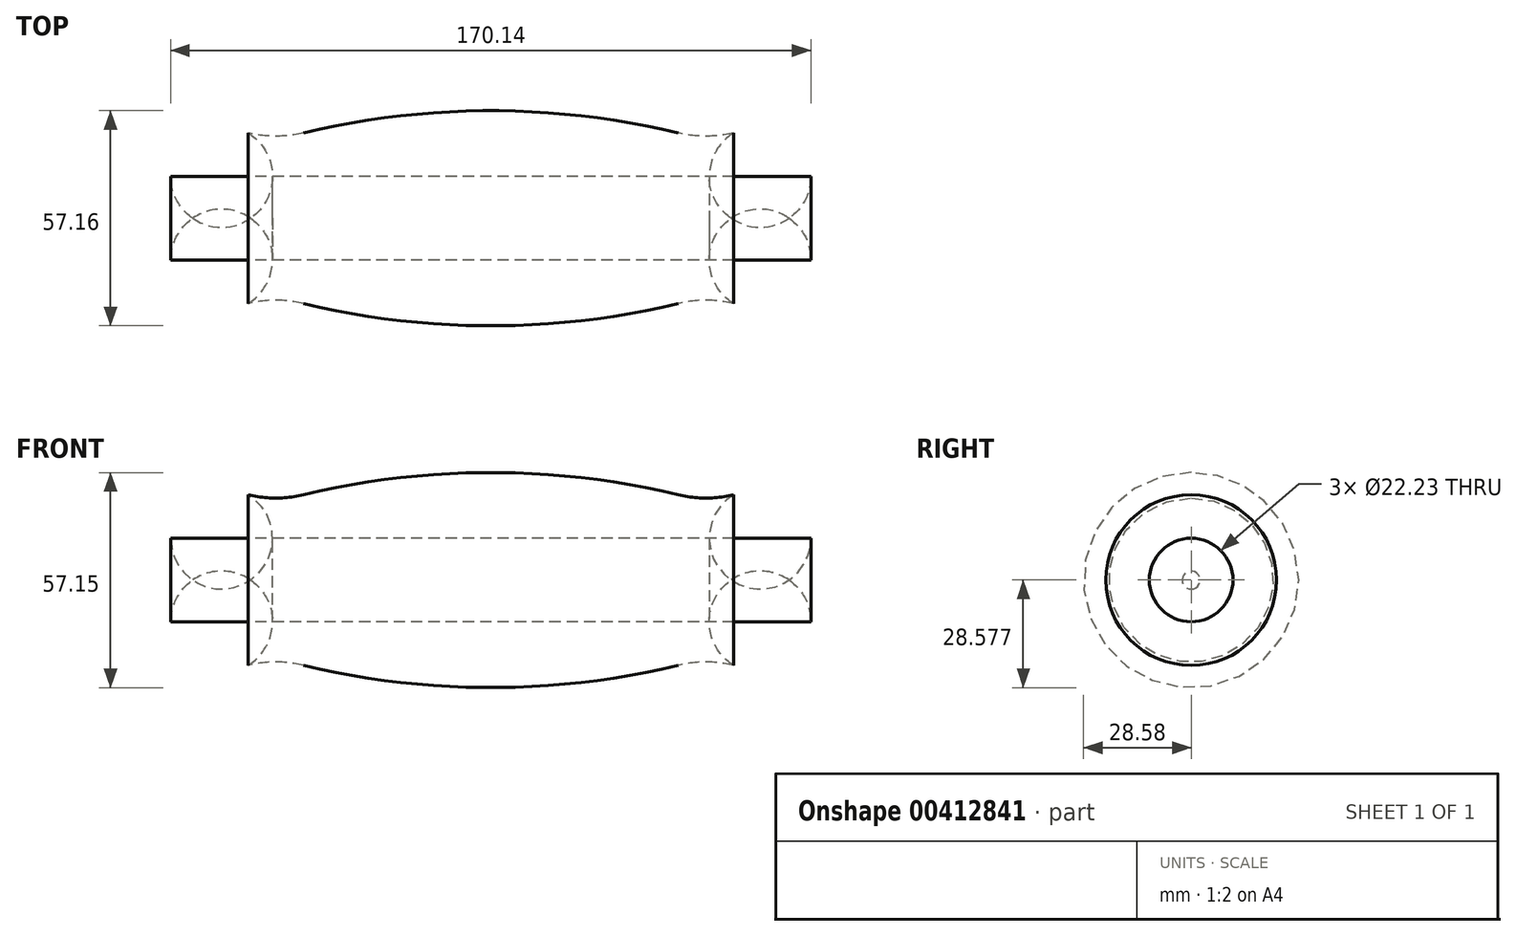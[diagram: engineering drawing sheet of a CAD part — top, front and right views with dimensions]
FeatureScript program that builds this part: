
annotation { "Feature Type Name" : "Feature", "Feature Type Description" : "" }
export const myFeature = defineFeature(function(context is Context, id is Id, definition is map)
    precondition{}
    {
        {
            var Q0;
            Q0=qCreatedBy(makeId("Front.planeOp"),FACE);
            var sketch = newSketch(context, id + "F0", { "sketchPlane" : qUnion([Q0])});
            skLineSegment(sketch, "E0", {"start": v(-49.73, 0) * mm, "end": v(12.26, 0) * mm, "construction": true});
            skArc(sketch, "E1", {"start": v(-49.73, 11.57) * mm, "mid": v(-25.04, 15.98) * mm, "end": v(0, 17.46) * mm});
            skArc(sketch, "E2", {"start": v(-49.73, 11.57) * mm, "mid": v(-57.15, 10.69) * mm, "end": v(-64.57, 11.57) * mm});
            skArc(sketch, "E3", {"start": v(-64.57, 11.57) * mm, "mid": v(-78.2, 11.77) * mm, "end": v(-85.07, 0) * mm});
            skLineSegment(sketch, "E4", {"start": v(-41.18, -11.11) * mm, "end": v(0, -11.11) * mm, "construction": true});
            skLineSegment(sketch, "E5", {"start": v(0, -11.11) * mm, "end": v(0, 44.87) * mm, "construction": true});
            skLineSegment(sketch, "E6", {"start": v(-85.07, 0) * mm, "end": v(0, 0) * mm});
            skArc(sketch, "E7.MirrorCS", {"start": v(49.73, 11.57) * mm, "mid": v(25.04, 15.98) * mm, "end": v(0, 17.46) * mm});
            skArc(sketch, "E8.MirrorCS", {"start": v(49.73, 11.57) * mm, "mid": v(57.15, 10.69) * mm, "end": v(64.57, 11.57) * mm});
            skArc(sketch, "E9.MirrorCS", {"start": v(64.57, 11.57) * mm, "mid": v(78.2, 11.77) * mm, "end": v(85.07, 0) * mm});
            skLineSegment(sketch, "E10.MirrorCS", {"start": v(85.07, 0) * mm, "end": v(0, 0) * mm});
            skSolve(sketch);
        }
        {
            var Q0;
            Q0 = qSketchRegion(id + "F0", true);
            var Q1;
            Q1=sQuery(id+"F0.wireOp",EDGE,"E4");
            revolve(context, id + "F1", {"entities" : qUnion([Q0]), "axis" : qUnion([Q1]), "revolveType" : RevolveType.FULL});
        }
    });
